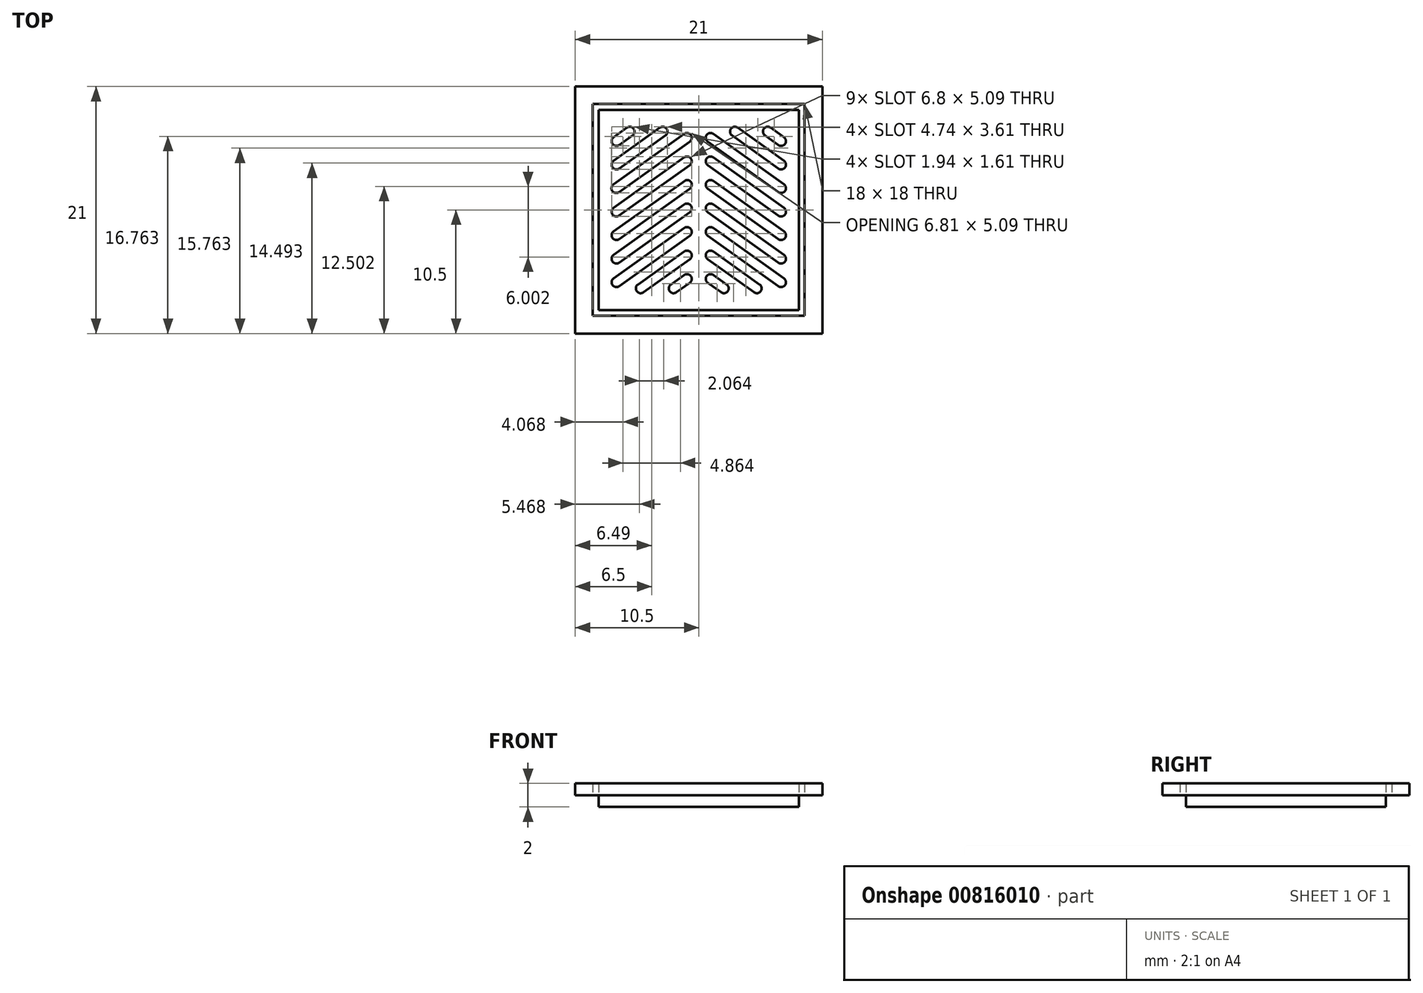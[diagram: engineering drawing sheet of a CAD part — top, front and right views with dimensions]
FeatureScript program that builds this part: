
annotation { "Feature Type Name" : "Feature", "Feature Type Description" : "" }
export const myFeature = defineFeature(function(context is Context, id is Id, definition is map)
    precondition{}
    {
        {
            var Q0;
            Q0=qCreatedBy(makeId("Top.planeOp"),FACE);
            var sketch = newSketch(context, id + "F0", { "sketchPlane" : qUnion([Q0])});
            skLineSegment(sketch, "E0.bottom", {"start": v(0, 0) * mm, "end": v(21, 0) * mm});
            skLineSegment(sketch, "E0.top", {"start": v(0, 21) * mm, "end": v(21, 21) * mm});
            skLineSegment(sketch, "E0.left", {"start": v(0, 0) * mm, "end": v(0, 21) * mm});
            skLineSegment(sketch, "E0.right", {"start": v(21, 0) * mm, "end": v(21, 21) * mm});
            skLineSegment(sketch, "E1.bottom", {"start": v(0, 0) * mm, "end": v(1.5, 0) * mm});
            skLineSegment(sketch, "E1.left", {"start": v(0, 0) * mm, "end": v(0, 1.5) * mm});
            skLineSegment(sketch, "E2.bottom", {"start": v(1.5, 1.5) * mm, "end": v(19.5, 1.5) * mm});
            skLineSegment(sketch, "E2.top", {"start": v(1.5, 19.5) * mm, "end": v(19.5, 19.5) * mm});
            skLineSegment(sketch, "E2.left", {"start": v(1.5, 1.5) * mm, "end": v(1.5, 19.5) * mm});
            skLineSegment(sketch, "E2.right", {"start": v(19.5, 1.5) * mm, "end": v(19.5, 19.5) * mm});
            skLineSegment(sketch, "E3.bottom", {"start": v(1.5, 1.5) * mm, "end": v(2, 1.5) * mm});
            skLineSegment(sketch, "E3.left", {"start": v(1.5, 1.5) * mm, "end": v(1.5, 2) * mm});
            skLineSegment(sketch, "E4.bottom", {"start": v(2, 2) * mm, "end": v(19, 2) * mm});
            skLineSegment(sketch, "E4.top", {"start": v(2, 19) * mm, "end": v(19, 19) * mm});
            skLineSegment(sketch, "E4.left", {"start": v(2, 2) * mm, "end": v(2, 19) * mm});
            skLineSegment(sketch, "E4.right", {"start": v(19, 2) * mm, "end": v(19, 19) * mm});
            skLineSegment(sketch, "E5.bottom", {"start": v(2, 2) * mm, "end": v(3, 2) * mm});
            skLineSegment(sketch, "E5.left", {"start": v(2, 2) * mm, "end": v(2, 3.5) * mm});
            skPoint(sketch, "E6.end.orphan", {"position": v(11, 13.28) * mm});
            skLineSegment(sketch, "E7", {"start": v(3.74, 4.03) * mm, "end": v(9.74, 8.31) * mm});
            skLineSegment(sketch, "E8", {"start": v(9.26, 8.97) * mm, "end": v(3.26, 4.69) * mm});
            skLineSegment(sketch, "E9", {"start": v(9.74, 4.31) * mm, "end": v(8.6, 3.5) * mm});
            skLineSegment(sketch, "E10", {"start": v(9.26, 4.97) * mm, "end": v(8.13, 4.16) * mm});
            skLineSegment(sketch, "E11", {"start": v(9.74, 6.31) * mm, "end": v(5.8, 3.5) * mm});
            skLineSegment(sketch, "E12", {"start": v(9.26, 6.97) * mm, "end": v(5.33, 4.16) * mm});
            skLineSegment(sketch, "E13", {"start": v(9.74, 10.31) * mm, "end": v(3.74, 6.03) * mm});
            skLineSegment(sketch, "E14", {"start": v(3.26, 6.69) * mm, "end": v(9.26, 10.97) * mm});
            skLineSegment(sketch, "E15", {"start": v(9.74, 12.31) * mm, "end": v(3.74, 8.03) * mm});
            skLineSegment(sketch, "E16", {"start": v(9.74, 14.31) * mm, "end": v(3.72, 10.02) * mm});
            skLineSegment(sketch, "E17", {"start": v(3.26, 10.69) * mm, "end": v(9.3, 15) * mm});
            skLineSegment(sketch, "E18", {"start": v(9.73, 16.3) * mm, "end": v(3.73, 12.02) * mm});
            skLineSegment(sketch, "E19", {"start": v(3.25, 12.68) * mm, "end": v(9.26, 16.97) * mm});
            skLineSegment(sketch, "E20", {"start": v(3.26, 14.69) * mm, "end": v(7.2, 17.5) * mm});
            skLineSegment(sketch, "E21", {"start": v(3.26, 16.69) * mm, "end": v(4.4, 17.5) * mm});
            skLineSegment(sketch, "E22", {"start": v(3.74, 16.03) * mm, "end": v(4.87, 16.84) * mm});
            skLineSegment(sketch, "E23", {"start": v(2, 2) * mm, "end": v(3.5, 2) * mm});
            skArc(sketch, "E24", {"start": v(3.26, 4.69) * mm, "mid": v(3.17, 4.12) * mm, "end": v(3.74, 4.03) * mm});
            skArc(sketch, "E25", {"start": v(3.26, 6.69) * mm, "mid": v(3.17, 6.12) * mm, "end": v(3.74, 6.03) * mm});
            skArc(sketch, "E26", {"start": v(9.74, 10.31) * mm, "mid": v(9.83, 10.88) * mm, "end": v(9.26, 10.97) * mm});
            skArc(sketch, "E27", {"start": v(9.74, 8.31) * mm, "mid": v(9.83, 8.88) * mm, "end": v(9.26, 8.97) * mm});
            skArc(sketch, "E28", {"start": v(3.26, 10.69) * mm, "mid": v(3.16, 10.13) * mm, "end": v(3.72, 10.02) * mm});
            skArc(sketch, "E29", {"start": v(3.25, 12.68) * mm, "mid": v(3.16, 12.11) * mm, "end": v(3.73, 12.02) * mm});
            skArc(sketch, "E30", {"start": v(3.26, 14.69) * mm, "mid": v(3.17, 14.12) * mm, "end": v(3.74, 14.03) * mm});
            skArc(sketch, "E31", {"start": v(3.26, 16.69) * mm, "mid": v(3.17, 16.12) * mm, "end": v(3.74, 16.03) * mm});
            skArc(sketch, "E32", {"start": v(9.73, 16.3) * mm, "mid": v(9.82, 16.87) * mm, "end": v(9.26, 16.97) * mm});
            skLineSegment(sketch, "E33", {"start": v(3.26, 8.69) * mm, "end": v(9.34, 13.02) * mm});
            skArc(sketch, "E34", {"start": v(9.74, 14.31) * mm, "mid": v(9.85, 14.86) * mm, "end": v(9.3, 15) * mm});
            skArc(sketch, "E35", {"start": v(9.74, 12.31) * mm, "mid": v(9.86, 12.84) * mm, "end": v(9.34, 13.02) * mm});
            skArc(sketch, "E36", {"start": v(3.26, 8.69) * mm, "mid": v(3.17, 8.12) * mm, "end": v(3.74, 8.03) * mm});
            skLineSegment(sketch, "E37", {"start": v(3.26, 8.69) * mm, "end": v(3.26, 8.69) * mm});
            skLineSegment(sketch, "E38.trimOffspring", {"start": v(3.74, 14.03) * mm, "end": v(7.67, 16.84) * mm});
            skLineSegment(sketch, "E39", {"start": v(9.26, 16.97) * mm, "end": v(9.26, 16.97) * mm});
            skLineSegment(sketch, "E40", {"start": v(9.25, 16.96) * mm, "end": v(9.26, 16.97) * mm});
            skArc(sketch, "E41", {"start": v(9.74, 6.31) * mm, "mid": v(9.83, 6.88) * mm, "end": v(9.26, 6.97) * mm});
            skArc(sketch, "E42", {"start": v(9.74, 4.31) * mm, "mid": v(9.83, 4.88) * mm, "end": v(9.26, 4.97) * mm});
            skArc(sketch, "E43", {"start": v(4.87, 16.84) * mm, "mid": v(4.97, 17.4) * mm, "end": v(4.4, 17.5) * mm});
            skArc(sketch, "E44", {"start": v(7.67, 16.84) * mm, "mid": v(7.77, 17.4) * mm, "end": v(7.2, 17.5) * mm});
            skPoint(sketch, "E45.orphan", {"position": v(7.67, 16.84) * mm});
            skArc(sketch, "E46", {"start": v(8.13, 4.16) * mm, "mid": v(8.03, 3.6) * mm, "end": v(8.6, 3.5) * mm});
            skArc(sketch, "E47", {"start": v(5.33, 4.16) * mm, "mid": v(5.23, 3.6) * mm, "end": v(5.8, 3.5) * mm});
            skPoint(sketch, "E48.end.orphan", {"position": v(5.33, 4.16) * mm});
            skLineSegment(sketch, "E49", {"start": v(17.26, 4.03) * mm, "end": v(11.26, 8.31) * mm});
            skLineSegment(sketch, "E50", {"start": v(11.74, 8.97) * mm, "end": v(17.74, 4.69) * mm});
            skLineSegment(sketch, "E51", {"start": v(17.26, 6.03) * mm, "end": v(11.26, 10.31) * mm});
            skLineSegment(sketch, "E52", {"start": v(11.74, 10.97) * mm, "end": v(17.74, 6.69) * mm});
            skLineSegment(sketch, "E53", {"start": v(17.26, 8.03) * mm, "end": v(11.26, 12.31) * mm});
            skLineSegment(sketch, "E54", {"start": v(17.74, 8.69) * mm, "end": v(11.74, 12.97) * mm});
            skLineSegment(sketch, "E55", {"start": v(11.26, 14.31) * mm, "end": v(17.26, 10.03) * mm});
            skLineSegment(sketch, "E56", {"start": v(17.74, 10.69) * mm, "end": v(11.74, 14.97) * mm});
            skLineSegment(sketch, "E57", {"start": v(11.26, 16.31) * mm, "end": v(17.26, 12.03) * mm});
            skLineSegment(sketch, "E58", {"start": v(17.74, 12.69) * mm, "end": v(11.74, 16.97) * mm});
            skLineSegment(sketch, "E59", {"start": v(17.26, 14.03) * mm, "end": v(13.33, 16.84) * mm});
            skLineSegment(sketch, "E60", {"start": v(17.74, 14.69) * mm, "end": v(13.8, 17.5) * mm});
            skLineSegment(sketch, "E61", {"start": v(17.74, 16.69) * mm, "end": v(16.6, 17.5) * mm});
            skLineSegment(sketch, "E62", {"start": v(17.26, 16.03) * mm, "end": v(16.13, 16.84) * mm});
            skLineSegment(sketch, "E63", {"start": v(11.74, 6.97) * mm, "end": v(15.67, 4.16) * mm});
            skLineSegment(sketch, "E64", {"start": v(11.26, 6.31) * mm, "end": v(15.2, 3.5) * mm});
            skLineSegment(sketch, "E65", {"start": v(11.26, 4.31) * mm, "end": v(12.4, 3.5) * mm});
            skLineSegment(sketch, "E66", {"start": v(11.74, 4.97) * mm, "end": v(12.87, 4.16) * mm});
            skPoint(sketch, "E67.orphan", {"position": v(11, 3.5) * mm});
            skLineSegment(sketch, "E68", {"start": v(19, 2) * mm, "end": v(17.5, 2) * mm});
            skLineSegment(sketch, "E69", {"start": v(11, 2) * mm, "end": v(11.5, 2) * mm});
            skPoint(sketch, "E70.endSnap0", {"position": v(10.5, 19.5) * mm});
            skPoint(sketch, "E71.orphan", {"position": v(11.5, 19.5) * mm});
            skArc(sketch, "E72", {"start": v(17.26, 4.03) * mm, "mid": v(17.83, 4.12) * mm, "end": v(17.74, 4.69) * mm});
            skArc(sketch, "E73", {"start": v(17.26, 6.03) * mm, "mid": v(17.83, 6.12) * mm, "end": v(17.74, 6.69) * mm});
            skArc(sketch, "E74", {"start": v(17.26, 8.03) * mm, "mid": v(17.83, 8.12) * mm, "end": v(17.74, 8.69) * mm});
            skArc(sketch, "E75", {"start": v(17.26, 10.03) * mm, "mid": v(17.83, 10.12) * mm, "end": v(17.74, 10.69) * mm});
            skArc(sketch, "E76", {"start": v(17.26, 12.03) * mm, "mid": v(17.83, 12.12) * mm, "end": v(17.74, 12.69) * mm});
            skArc(sketch, "E77", {"start": v(17.26, 14.03) * mm, "mid": v(17.83, 14.12) * mm, "end": v(17.74, 14.69) * mm});
            skArc(sketch, "E78", {"start": v(17.26, 16.03) * mm, "mid": v(17.83, 16.12) * mm, "end": v(17.74, 16.69) * mm});
            skPoint(sketch, "E79.orphan", {"position": v(17.5, 16.86) * mm});
            skPoint(sketch, "E80.start.orphan", {"position": v(17.5, 3.86) * mm});
            skArc(sketch, "E81", {"start": v(11.74, 4.97) * mm, "mid": v(11.17, 4.88) * mm, "end": v(11.26, 4.31) * mm});
            skArc(sketch, "E82", {"start": v(11.74, 6.97) * mm, "mid": v(11.17, 6.88) * mm, "end": v(11.26, 6.31) * mm});
            skArc(sketch, "E83", {"start": v(11.74, 8.97) * mm, "mid": v(11.17, 8.88) * mm, "end": v(11.26, 8.31) * mm});
            skArc(sketch, "E84", {"start": v(11.74, 10.97) * mm, "mid": v(11.17, 10.88) * mm, "end": v(11.26, 10.31) * mm});
            skArc(sketch, "E85", {"start": v(11.74, 12.97) * mm, "mid": v(11.17, 12.88) * mm, "end": v(11.26, 12.31) * mm});
            skArc(sketch, "E86", {"start": v(11.74, 14.97) * mm, "mid": v(11.17, 14.88) * mm, "end": v(11.26, 14.31) * mm});
            skArc(sketch, "E87", {"start": v(11.74, 16.97) * mm, "mid": v(11.17, 16.88) * mm, "end": v(11.26, 16.31) * mm});
            skPoint(sketch, "E88.end.orphan", {"position": v(11, 17.5) * mm});
            skArc(sketch, "E89", {"start": v(13.8, 17.5) * mm, "mid": v(13.23, 17.4) * mm, "end": v(13.33, 16.84) * mm});
            skArc(sketch, "E90", {"start": v(16.6, 17.5) * mm, "mid": v(16.03, 17.4) * mm, "end": v(16.13, 16.84) * mm});
            skPoint(sketch, "E91.end.orphan", {"position": v(13.33, 16.84) * mm});
            skPoint(sketch, "E92.trimOffspring.start.orphan", {"position": v(12.4, 17.5) * mm});
            skArc(sketch, "E93", {"start": v(15.2, 3.5) * mm, "mid": v(15.77, 3.6) * mm, "end": v(15.67, 4.16) * mm});
            skArc(sketch, "E94", {"start": v(12.4, 3.5) * mm, "mid": v(12.97, 3.6) * mm, "end": v(12.87, 4.16) * mm});
            skSolve(sketch);
        }
        {
            var Q0;
            Q0=makeQuery(id+"F0.imprint","IMPRINT",FACE,{"disambiguationData":[TD([[makeQuery(id+"F0.imprint","IMPRINT",EDGE,{"derivedFrom":sQuery(id+"F0.wireOp",EDGE,"E4.top")}),-1.0]])]});
            var Q1;
            Q1=makeQuery(id+"F0.imprint","IMPRINT",FACE,{"disambiguationData":[TD([[makeQuery(id+"F0.imprint","IMPRINT",EDGE,{"derivedFrom":sQuery(id+"F0.wireOp",EDGE,"E0.bottom")}),1.0]])]});
            extrude(context, id + "F1", {"entities" : qUnion([Q0, Q1]), "depth" : 1 * mm, "offsetDistance" : 25 * mm});
        }
        {
            var Q0;
            Q0=makeQuery(id+"F1.opExtrude","CAP_FACE",FACE,{"disambiguationData":[OSD([sQuery(id+"F0.wireOp",EDGE,"E4.bottom"),sQuery(id+"F0.wireOp",EDGE,"E4.top"),sQuery(id+"F0.wireOp",EDGE,"E4.left"),sQuery(id+"F0.wireOp",EDGE,"E4.right"),sQuery(id+"F0.wireOp",EDGE,"E5.left"),sQuery(id+"F0.wireOp",EDGE,"E7"),sQuery(id+"F0.wireOp",EDGE,"E8"),sQuery(id+"F0.wireOp",EDGE,"E9"),sQuery(id+"F0.wireOp",EDGE,"E10"),sQuery(id+"F0.wireOp",EDGE,"E11"),sQuery(id+"F0.wireOp",EDGE,"E12"),sQuery(id+"F0.wireOp",EDGE,"E13"),sQuery(id+"F0.wireOp",EDGE,"E14"),sQuery(id+"F0.wireOp",EDGE,"E15"),sQuery(id+"F0.wireOp",EDGE,"E16"),sQuery(id+"F0.wireOp",EDGE,"E17"),sQuery(id+"F0.wireOp",EDGE,"E18"),sQuery(id+"F0.wireOp",EDGE,"E19"),sQuery(id+"F0.wireOp",EDGE,"E20"),sQuery(id+"F0.wireOp",EDGE,"E21"),sQuery(id+"F0.wireOp",EDGE,"E22"),sQuery(id+"F0.wireOp",EDGE,"E23"),sQuery(id+"F0.wireOp",EDGE,"E24"),sQuery(id+"F0.wireOp",EDGE,"E25"),sQuery(id+"F0.wireOp",EDGE,"E26"),sQuery(id+"F0.wireOp",EDGE,"E27"),sQuery(id+"F0.wireOp",EDGE,"E28"),sQuery(id+"F0.wireOp",EDGE,"E29"),sQuery(id+"F0.wireOp",EDGE,"E30"),sQuery(id+"F0.wireOp",EDGE,"E31"),sQuery(id+"F0.wireOp",EDGE,"E32"),sQuery(id+"F0.wireOp",EDGE,"E33"),sQuery(id+"F0.wireOp",EDGE,"E34"),sQuery(id+"F0.wireOp",EDGE,"E35"),sQuery(id+"F0.wireOp",EDGE,"E36"),sQuery(id+"F0.wireOp",EDGE,"E37"),sQuery(id+"F0.wireOp",EDGE,"E38.trimOffspring"),sQuery(id+"F0.wireOp",EDGE,"E40"),sQuery(id+"F0.wireOp",EDGE,"E41"),sQuery(id+"F0.wireOp",EDGE,"E42"),sQuery(id+"F0.wireOp",EDGE,"E43"),sQuery(id+"F0.wireOp",EDGE,"E44"),sQuery(id+"F0.wireOp",EDGE,"E46"),sQuery(id+"F0.wireOp",EDGE,"E47"),sQuery(id+"F0.wireOp",EDGE,"E49"),sQuery(id+"F0.wireOp",EDGE,"E50"),sQuery(id+"F0.wireOp",EDGE,"E51"),sQuery(id+"F0.wireOp",EDGE,"E52"),sQuery(id+"F0.wireOp",EDGE,"E53"),sQuery(id+"F0.wireOp",EDGE,"E54"),sQuery(id+"F0.wireOp",EDGE,"E55"),sQuery(id+"F0.wireOp",EDGE,"E56"),sQuery(id+"F0.wireOp",EDGE,"E57"),sQuery(id+"F0.wireOp",EDGE,"E58"),sQuery(id+"F0.wireOp",EDGE,"E59"),sQuery(id+"F0.wireOp",EDGE,"E60"),sQuery(id+"F0.wireOp",EDGE,"E61"),sQuery(id+"F0.wireOp",EDGE,"E62"),sQuery(id+"F0.wireOp",EDGE,"E63"),sQuery(id+"F0.wireOp",EDGE,"E64"),sQuery(id+"F0.wireOp",EDGE,"E65"),sQuery(id+"F0.wireOp",EDGE,"E66"),sQuery(id+"F0.wireOp",EDGE,"E68"),sQuery(id+"F0.wireOp",EDGE,"E69"),sQuery(id+"F0.wireOp",EDGE,"E72"),sQuery(id+"F0.wireOp",EDGE,"E73"),sQuery(id+"F0.wireOp",EDGE,"E74"),sQuery(id+"F0.wireOp",EDGE,"E75"),sQuery(id+"F0.wireOp",EDGE,"E76"),sQuery(id+"F0.wireOp",EDGE,"E77"),sQuery(id+"F0.wireOp",EDGE,"E78"),sQuery(id+"F0.wireOp",EDGE,"E81"),sQuery(id+"F0.wireOp",EDGE,"E82"),sQuery(id+"F0.wireOp",EDGE,"E83"),sQuery(id+"F0.wireOp",EDGE,"E84"),sQuery(id+"F0.wireOp",EDGE,"E85"),sQuery(id+"F0.wireOp",EDGE,"E86"),sQuery(id+"F0.wireOp",EDGE,"E87"),sQuery(id+"F0.wireOp",EDGE,"E89"),sQuery(id+"F0.wireOp",EDGE,"E90"),sQuery(id+"F0.wireOp",EDGE,"E93"),sQuery(id+"F0.wireOp",EDGE,"E94")])],"isStart":true});
            extrude(context, id + "F2", {"entities" : qUnion([Q0]), "operationType" : NewBodyOperationType.ADD, "depth" : 1 * mm, "offsetDistance" : 25 * mm});
        }
    });
